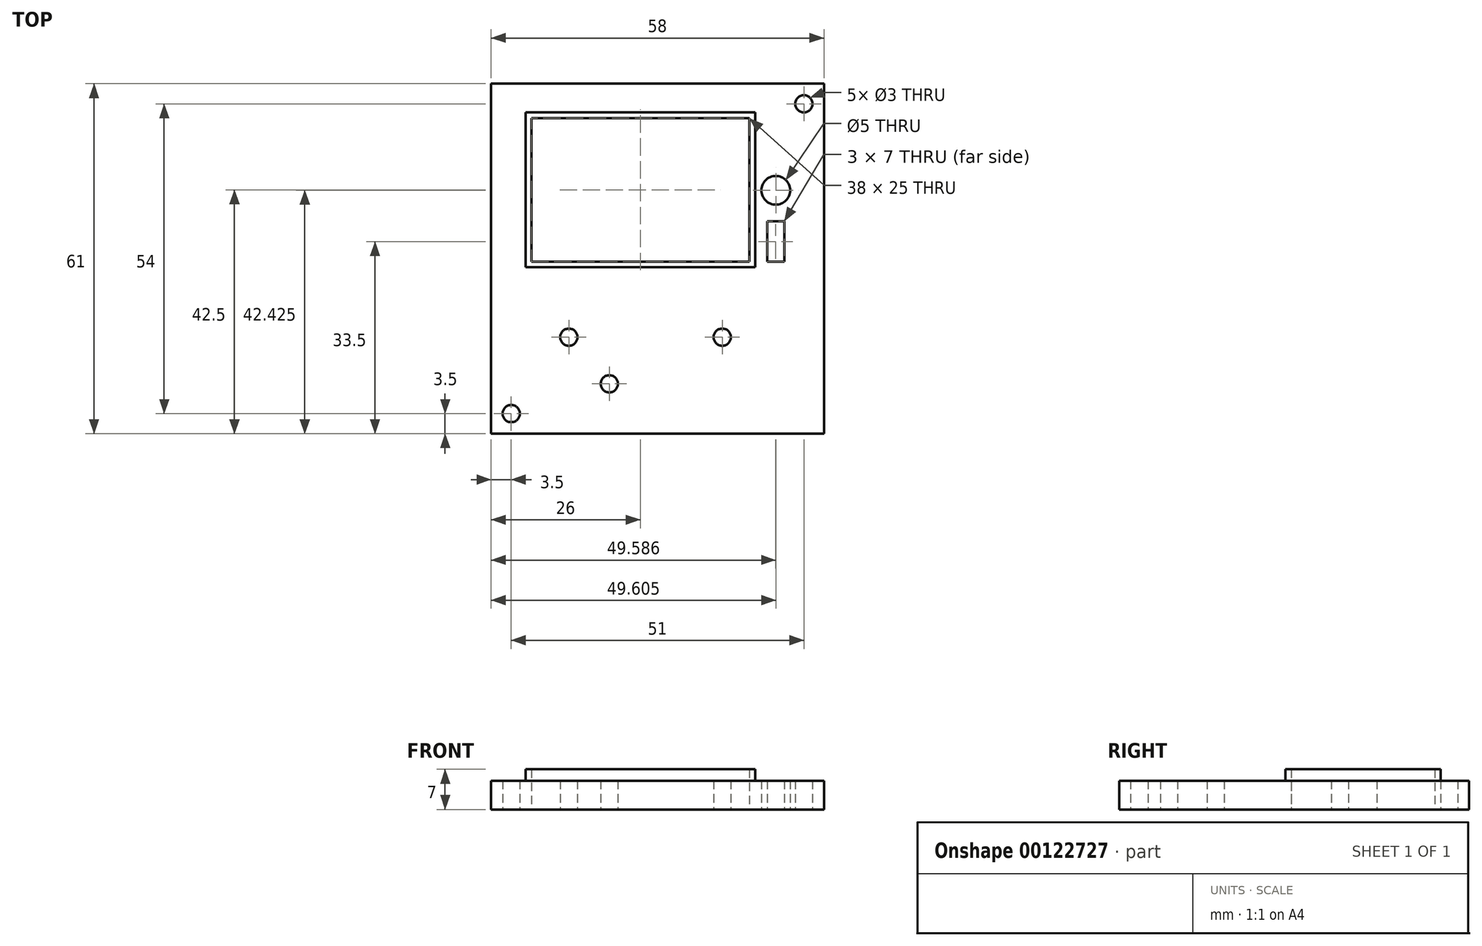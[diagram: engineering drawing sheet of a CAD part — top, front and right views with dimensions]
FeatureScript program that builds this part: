
annotation { "Feature Type Name" : "Feature", "Feature Type Description" : "" }
export const myFeature = defineFeature(function(context is Context, id is Id, definition is map)
    precondition{}
    {
        {
            var Q0;
            Q0=qCreatedBy(makeId("Top.planeOp"),FACE);
            var sketch = newSketch(context, id + "F0", { "sketchPlane" : qUnion([Q0])});
            skLineSegment(sketch, "E0.bottom", {"start": v(0, 0) * mm, "end": v(58, 0) * mm});
            skLineSegment(sketch, "E0.top", {"start": v(0, -61) * mm, "end": v(58, -61) * mm});
            skLineSegment(sketch, "E0.left", {"start": v(0, 0) * mm, "end": v(0, -61) * mm});
            skLineSegment(sketch, "E0.right", {"start": v(58, 0) * mm, "end": v(58, -61) * mm});
            skLineSegment(sketch, "E1.bottom", {"start": v(7, -6) * mm, "end": v(45, -6) * mm});
            skLineSegment(sketch, "E1.top", {"start": v(7, -31) * mm, "end": v(45, -31) * mm});
            skLineSegment(sketch, "E1.left", {"start": v(7, -6) * mm, "end": v(7, -31) * mm});
            skLineSegment(sketch, "E1.right", {"start": v(45, -6) * mm, "end": v(45, -31) * mm});
            skCircle(sketch, "E2", {"center": v(13.54, -44.17) * mm, "radius": 4 * mm, "construction": true});
            skCircle(sketch, "E3", {"center": v(3.5, -57.5) * mm, "radius": 1.5 * mm});
            skCircle(sketch, "E4", {"center": v(40.28, -44.17) * mm, "radius": 6 * mm, "construction": true});
            skLineSegment(sketch, "E5.bottom", {"start": v(48.09, -24) * mm, "end": v(51.09, -24) * mm});
            skLineSegment(sketch, "E5.top", {"start": v(48.09, -31) * mm, "end": v(51.09, -31) * mm});
            skLineSegment(sketch, "E5.left", {"start": v(48.09, -24) * mm, "end": v(48.09, -31) * mm});
            skLineSegment(sketch, "E5.right", {"start": v(51.09, -24) * mm, "end": v(51.09, -31) * mm});
            skCircle(sketch, "E6", {"center": v(54.5, -3.5) * mm, "radius": 1.5 * mm});
            skCircle(sketch, "E7", {"center": v(20.6, -52.3) * mm, "radius": 1.5 * mm});
            skCircle(sketch, "E8", {"center": v(49.6, -18.57) * mm, "radius": 2.5 * mm});
            skCircle(sketch, "E9", {"center": v(13.54, -44.17) * mm, "radius": 1.5 * mm});
            skCircle(sketch, "E10", {"center": v(40.28, -44.17) * mm, "radius": 1.5 * mm});
            skSolve(sketch);
        }
        {
            var Q0;
            Q0=makeQuery(id+"F0.imprint","IMPRINT",FACE,{"disambiguationData":[TD([[makeQuery(id+"F0.imprint","IMPRINT",EDGE,{"derivedFrom":sQuery(id+"F0.wireOp",EDGE,"E0.bottom")}),-1.0]])]});
            extrude(context, id + "F1", {"entities" : qUnion([Q0]), "depth" : 5 * mm});
        }
        {
            var Q0;
            Q0=makeQuery(id+"F1.opExtrude","CAP_FACE",FACE,{"disambiguationData":[OSD([sQuery(id+"F0.wireOp",EDGE,"E0.bottom"),sQuery(id+"F0.wireOp",EDGE,"E0.top"),sQuery(id+"F0.wireOp",EDGE,"E0.left"),sQuery(id+"F0.wireOp",EDGE,"E0.right"),sQuery(id+"F0.wireOp",EDGE,"E1.bottom"),sQuery(id+"F0.wireOp",EDGE,"E1.top"),sQuery(id+"F0.wireOp",EDGE,"E1.left"),sQuery(id+"F0.wireOp",EDGE,"E1.right"),sQuery(id+"F0.wireOp",EDGE,"E3"),sQuery(id+"F0.wireOp",EDGE,"E5.bottom"),sQuery(id+"F0.wireOp",EDGE,"E5.top"),sQuery(id+"F0.wireOp",EDGE,"E5.left"),sQuery(id+"F0.wireOp",EDGE,"E5.right"),sQuery(id+"F0.wireOp",EDGE,"E6"),sQuery(id+"F0.wireOp",EDGE,"E7"),sQuery(id+"F0.wireOp",EDGE,"E8"),sQuery(id+"F0.wireOp",EDGE,"E9"),sQuery(id+"F0.wireOp",EDGE,"E10")])],"isStart":false});
            var sketch = newSketch(context, id + "F2", { "sketchPlane" : qUnion([Q0])});
            skLineSegment(sketch, "E11.bottom", {"start": v(7, -6) * mm, "end": v(45, -6) * mm});
            skLineSegment(sketch, "E11.top", {"start": v(7, -31) * mm, "end": v(45, -31) * mm});
            skLineSegment(sketch, "E11.left", {"start": v(7, -6) * mm, "end": v(7, -31) * mm});
            skLineSegment(sketch, "E11.right", {"start": v(45, -6) * mm, "end": v(45, -31) * mm});
            skLineSegment(sketch, "E12.bottom", {"start": v(6, -5) * mm, "end": v(46, -5) * mm});
            skLineSegment(sketch, "E12.top", {"start": v(6, -32) * mm, "end": v(46, -32) * mm});
            skLineSegment(sketch, "E12.left", {"start": v(6, -5) * mm, "end": v(6, -32) * mm});
            skLineSegment(sketch, "E12.right", {"start": v(46, -5) * mm, "end": v(46, -32) * mm});
            skSolve(sketch);
        }
        {
            var Q0;
            Q0=qSketchRegion(id+"F2",true);
            extrude(context, id + "F3", {"entities" : qUnion([Q0]), "operationType" : NewBodyOperationType.ADD, "depth" : 2 * mm});
        }
    });
